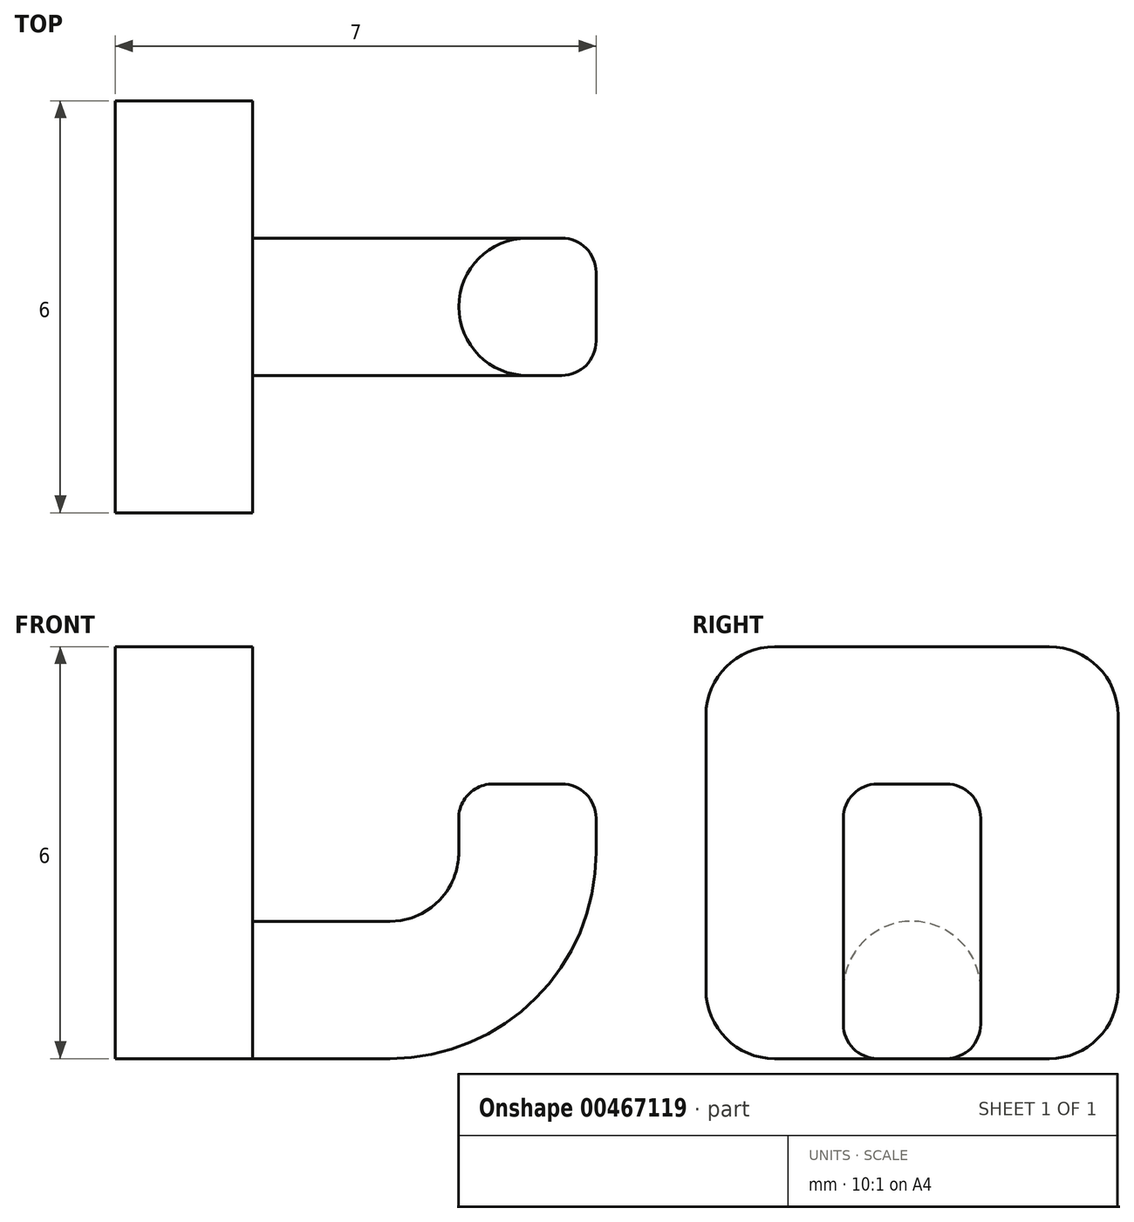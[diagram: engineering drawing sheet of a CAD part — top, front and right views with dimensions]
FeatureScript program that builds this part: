
annotation { "Feature Type Name" : "Feature", "Feature Type Description" : "" }
export const myFeature = defineFeature(function(context is Context, id is Id, definition is map)
    precondition{}
    {
        {
            var Q0;
            Q0=qCreatedBy(makeId("Front.planeOp"),FACE);
            var sketch = newSketch(context, id + "F0", { "sketchPlane" : qUnion([Q0])});
            skLineSegment(sketch, "E0", {"start": v(0, 0) * mm, "end": v(2, 0) * mm});
            skArc(sketch, "E1", {"start": v(2, 0) * mm, "mid": v(3.41, 0.59) * mm, "end": v(4, 2) * mm});
            skLineSegment(sketch, "E2", {"start": v(4, 2) * mm, "end": v(4, 3) * mm});
            skSolve(sketch);
        }
        {
            var Q0;
            Q0=qCreatedBy(makeId("Right.planeOp"),FACE);
            var sketch = newSketch(context, id + "F1", { "sketchPlane" : qUnion([Q0])});
            skArc(sketch, "E3", {"start": v(1, 0) * mm, "mid": v(0, 1) * mm, "end": v(-1, 0) * mm});
            skLineSegment(sketch, "E4.top", {"start": v(-1, -1) * mm, "end": v(1, -1) * mm});
            skLineSegment(sketch, "E4.left", {"start": v(-1, 0) * mm, "end": v(-1, -1) * mm});
            skLineSegment(sketch, "E4.right", {"start": v(1, 0) * mm, "end": v(1, -1) * mm});
            skSolve(sketch);
        }
        {
            var Q0;
            Q0 = qSketchRegion(id + "F1", true);
            var Q1;
            Q1=sQuery(id+"F0.wireOp",EDGE,"E0");
            var Q2;
            Q2=sQuery(id+"F0.wireOp",EDGE,"E1");
            var Q3;
            Q3=sQuery(id+"F0.wireOp",EDGE,"E2");
            sweep(context, id + "F2", {"profiles" : qUnion([Q0]), "path" : qUnion([Q1, Q2, Q3])});
        }
        {
            var Q0;
            Q0=makeQuery(id+"F2.opSweep","CAP_EDGE",EDGE,{"disambiguationData":[OSD([sQuery(id+"F0.wireOp",VERTEX,"E2.end"),sQuery(id+"F1.wireOp",EDGE,"E4.top")])],"isStart":false});
            var Q1;
            Q1=makeQuery(id+"F2.opSweep","CAP_EDGE",EDGE,{"disambiguationData":[OSD([sQuery(id+"F0.wireOp",VERTEX,"E2.end"),sQuery(id+"F1.wireOp",EDGE,"E3")])],"isStart":false});
            var Q2;
            Q2=makeQuery(id+"F2.opSweep","SWEPT_EDGE",EDGE,{"disambiguationData":[OSD([sQuery(id+"F0.wireOp",EDGE,"E1"),sQuery(id+"F1.wireOp",EDGE,"E4.top"),sQuery(id+"F1.wireOp",EDGE,"E4.left")])]});
            var Q3;
            Q3=makeQuery(id+"F2.opSweep","SWEPT_EDGE",EDGE,{"disambiguationData":[OSD([sQuery(id+"F0.wireOp",EDGE,"E1"),sQuery(id+"F1.wireOp",EDGE,"E4.top"),sQuery(id+"F1.wireOp",EDGE,"E4.right")])]});
            fillet(context, id + "F3", {"entities" : qUnion([Q0, Q1, Q2, Q3]), "radius" : 0.5 * mm, "tangentPropagation" : true, "allowEdgeOverflow" : false});
        }
        {
            var Q0;
            Q0=qCreatedBy(makeId("Top.planeOp"),FACE);
            var sketch = newSketch(context, id + "F4", { "sketchPlane" : qUnion([Q0])});
            skLineSegment(sketch, "E5.bottom", {"start": v(0, 3) * mm, "end": v(-2, 3) * mm});
            skLineSegment(sketch, "E5.top", {"start": v(0, -3) * mm, "end": v(-2, -3) * mm});
            skLineSegment(sketch, "E5.left", {"start": v(0, 3) * mm, "end": v(0, -3) * mm});
            skLineSegment(sketch, "E5.right", {"start": v(-2, 3) * mm, "end": v(-2, -3) * mm});
            skSolve(sketch);
        }
        {
            var Q0;
            Q0 = qSketchRegion(id + "F4", true);
            var Q1;
            Q1=makeQuery(id+"F2.opSweep","SWEPT_FACE",FACE,{"disambiguationData":[OSD([sQuery(id+"F0.wireOp",EDGE,"E0"),sQuery(id+"F1.wireOp",EDGE,"E4.top")])]});
            extrude(context, id + "F5", {"entities" : qUnion([Q0]), "operationType" : NewBodyOperationType.ADD, "depth" : 5 * mm, "hasSecondDirection" : true, "secondDirectionBound" : SecondDirectionBoundingType.UP_TO_SURFACE, "secondDirectionOppositeDirection" : true, "secondDirectionBoundEntityFace" : qUnion([Q1]), "secondDirectionDepth" : 25 * mm});
        }
        {
            var Q0;
            Q0=makeQuery(id+"F5.opExtrude","CAP_EDGE",EDGE,{"disambiguationData":[OSD([sQuery(id+"F4.wireOp",EDGE,"E5.top")])],"isStart":true});
            var Q1;
            Q1=makeQuery(id+"F5.opExtrude","CAP_EDGE",EDGE,{"disambiguationData":[OSD([sQuery(id+"F4.wireOp",EDGE,"E5.top")])],"isStart":false});
            var Q2;
            Q2=makeQuery(id+"F5.opExtrude","CAP_EDGE",EDGE,{"disambiguationData":[OSD([sQuery(id+"F4.wireOp",EDGE,"E5.bottom")])],"isStart":false});
            var Q3;
            Q3=makeQuery(id+"F5.opExtrude","CAP_EDGE",EDGE,{"disambiguationData":[OSD([sQuery(id+"F4.wireOp",EDGE,"E5.bottom")])],"isStart":true});
            fillet(context, id + "F6", {"entities" : qUnion([Q0, Q1, Q2, Q3]), "radius" : 1 * mm, "tangentPropagation" : true, "allowEdgeOverflow" : false});
        }
    });
